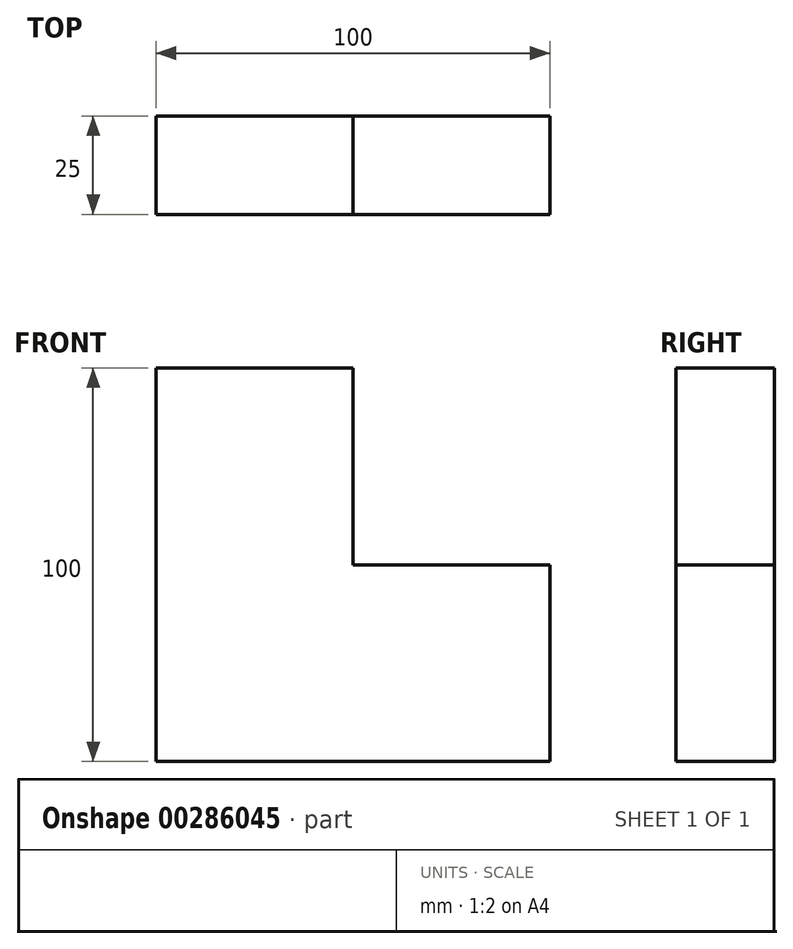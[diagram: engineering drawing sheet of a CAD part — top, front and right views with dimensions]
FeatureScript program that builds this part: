
annotation { "Feature Type Name" : "Feature", "Feature Type Description" : "" }
export const myFeature = defineFeature(function(context is Context, id is Id, definition is map)
    precondition{}
    {
        {
            var Q0;
            Q0=qCreatedBy(makeId("Front.planeOp"),FACE);
            var sketch = newSketch(context, id + "F0", { "sketchPlane" : qUnion([Q0])});
            skLineSegment(sketch, "E0.bottom", {"start": v(0, 0) * mm, "end": v(100, 0) * mm});
            skLineSegment(sketch, "E0.top", {"start": v(0, 100) * mm, "end": v(50, 100) * mm});
            skLineSegment(sketch, "E0.left", {"start": v(0, 0) * mm, "end": v(0, 100) * mm});
            skLineSegment(sketch, "E1.top", {"start": v(100, 50) * mm, "end": v(50, 50) * mm});
            skLineSegment(sketch, "E1.right", {"start": v(50, 100) * mm, "end": v(50, 50) * mm});
            skLineSegment(sketch, "E2", {"start": v(100, 50) * mm, "end": v(100, 0) * mm});
            skSolve(sketch);
        }
        {
            var Q0;
            Q0 = qSketchRegion(id + "F0", true);
            extrude(context, id + "F1", {"entities" : qUnion([Q0]), "depth" : 25 * mm});
        }
    });
